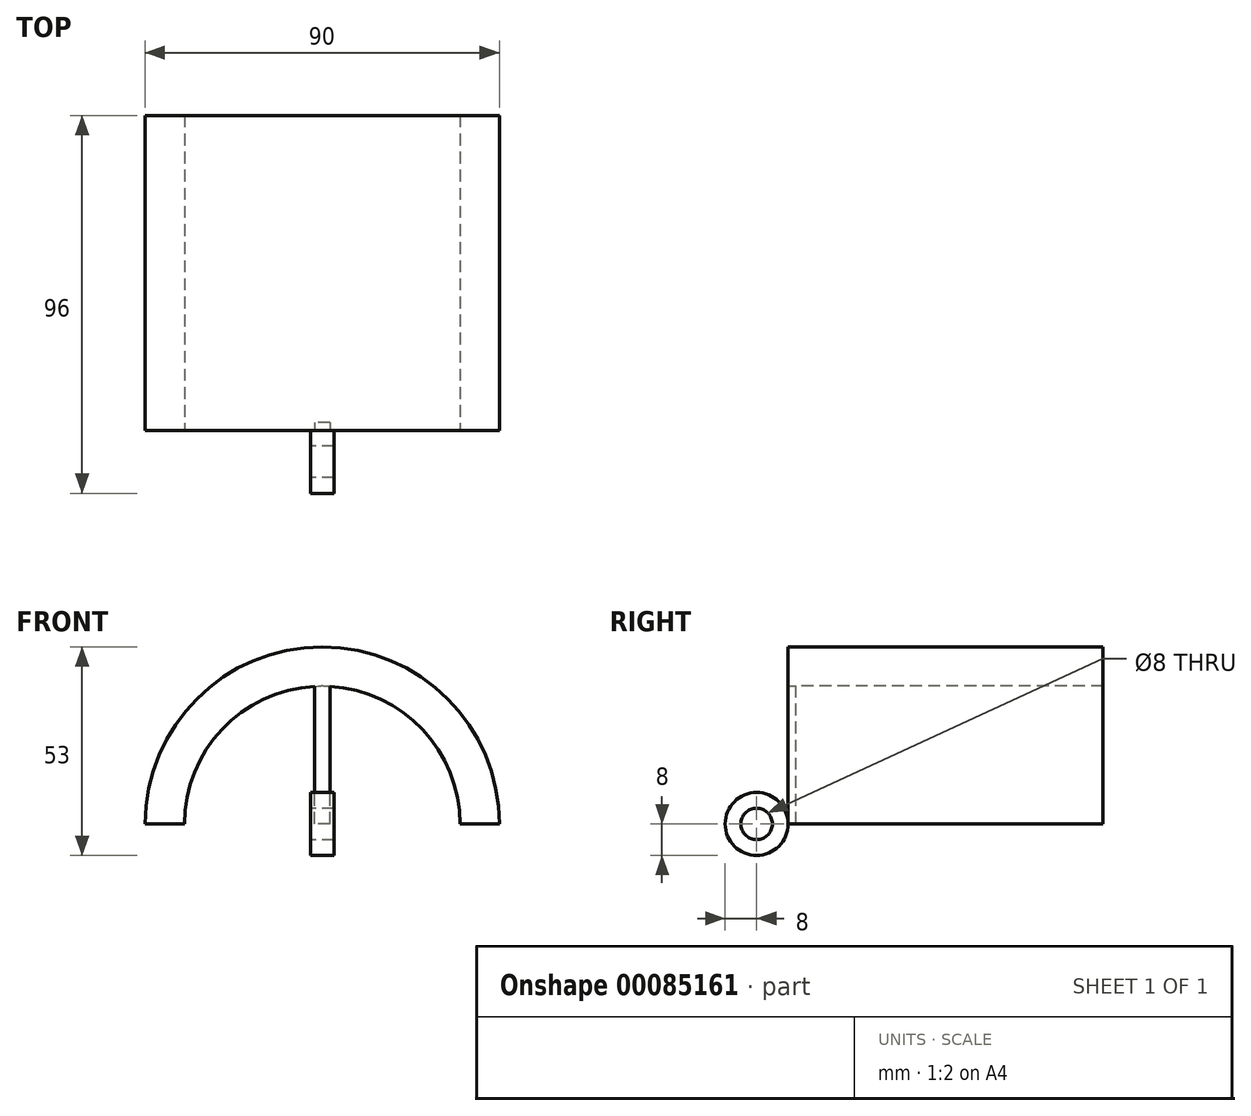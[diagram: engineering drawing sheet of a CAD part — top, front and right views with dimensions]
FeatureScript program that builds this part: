
annotation { "Feature Type Name" : "Feature", "Feature Type Description" : "" }
export const myFeature = defineFeature(function(context is Context, id is Id, definition is map)
    precondition{}
    {
        {
            var Q0;
            Q0=qCreatedBy(makeId("Front.planeOp"),FACE);
            var sketch = newSketch(context, id + "F0", { "sketchPlane" : qUnion([Q0])});
            skPoint(sketch, "E0.middle", {"position": v(0, 35) * mm});
            skArc(sketch, "E1", {"start": v(45, 0) * mm, "mid": v(0, 45) * mm, "end": v(-45, 0) * mm});
            skLineSegment(sketch, "E2", {"start": v(-45, 0) * mm, "end": v(-35, 0) * mm});
            skLineSegment(sketch, "E3", {"start": v(45, 0) * mm, "end": v(35, 0) * mm});
            skArc(sketch, "E4", {"start": v(35, 0) * mm, "mid": v(0, 35) * mm, "end": v(-35, 0) * mm});
            skLineSegment(sketch, "E5", {"start": v(0, 0) * mm, "end": v(-2, 0) * mm});
            skLineSegment(sketch, "E6", {"start": v(0, 0) * mm, "end": v(2, 0) * mm});
            skLineSegment(sketch, "E7", {"start": v(-2, 0) * mm, "end": v(-2, 34.94) * mm});
            skLineSegment(sketch, "E8", {"start": v(2, 0) * mm, "end": v(2, 34.94) * mm});
            skSolve(sketch);
        }
        {
            var Q0;
            Q0=qCreatedBy(makeId("Right.planeOp"),FACE);
            var sketch = newSketch(context, id + "F1", { "sketchPlane" : qUnion([Q0])});
            skLineSegment(sketch, "E9", {"start": v(0, 0) * mm, "end": v(-16, 0) * mm});
            skCircle(sketch, "E10", {"center": v(-8, 0) * mm, "radius": 8 * mm});
            skCircle(sketch, "E11", {"center": v(-8, 0) * mm, "radius": 4 * mm});
            skSolve(sketch);
        }
        {
            var Q0;
            Q0 = qSketchRegion(id + "F1", true);
            extrude(context, id + "F2", {"entities" : qUnion([Q0]), "endBound" : BoundingType.SYMMETRIC, "depth" : 6 * mm});
        }
        {
            var Q0;
            Q0=makeQuery(id+"F0.imprint","IMPRINT",FACE,{"disambiguationData":[TD([[makeQuery(id+"F0.imprint","IMPRINT",EDGE,{"derivedFrom":sQuery(id+"F0.wireOp",EDGE,"E1")}),1.0]])]});
            extrude(context, id + "F3", {"entities" : qUnion([Q0]), "oppositeDirection" : true, "depth" : 80 * mm});
        }
        {
            var Q0;
            Q0=qCreatedBy(makeId("Front.planeOp"),FACE);
            var sketch = newSketch(context, id + "F4", { "sketchPlane" : qUnion([Q0])});
            skArc(sketch, "E12", {"start": v(35, 0) * mm, "mid": v(0, 35) * mm, "end": v(-35, 0) * mm});
            skLineSegment(sketch, "E13", {"start": v(0, 0) * mm, "end": v(-2, 0) * mm});
            skLineSegment(sketch, "E14", {"start": v(0, 0) * mm, "end": v(2, 0) * mm});
            skLineSegment(sketch, "E15", {"start": v(-2, 0) * mm, "end": v(-2, 35) * mm});
            skLineSegment(sketch, "E16", {"start": v(2, 0) * mm, "end": v(2, 34.94) * mm});
            skSolve(sketch);
        }
        {
            var Q0;
            Q0 = qSketchRegion(id + "F4", true);
            extrude(context, id + "F5", {"entities" : qUnion([Q0]), "operationType" : NewBodyOperationType.ADD, "oppositeDirection" : true, "depth" : 2 * mm});
        }
    });
